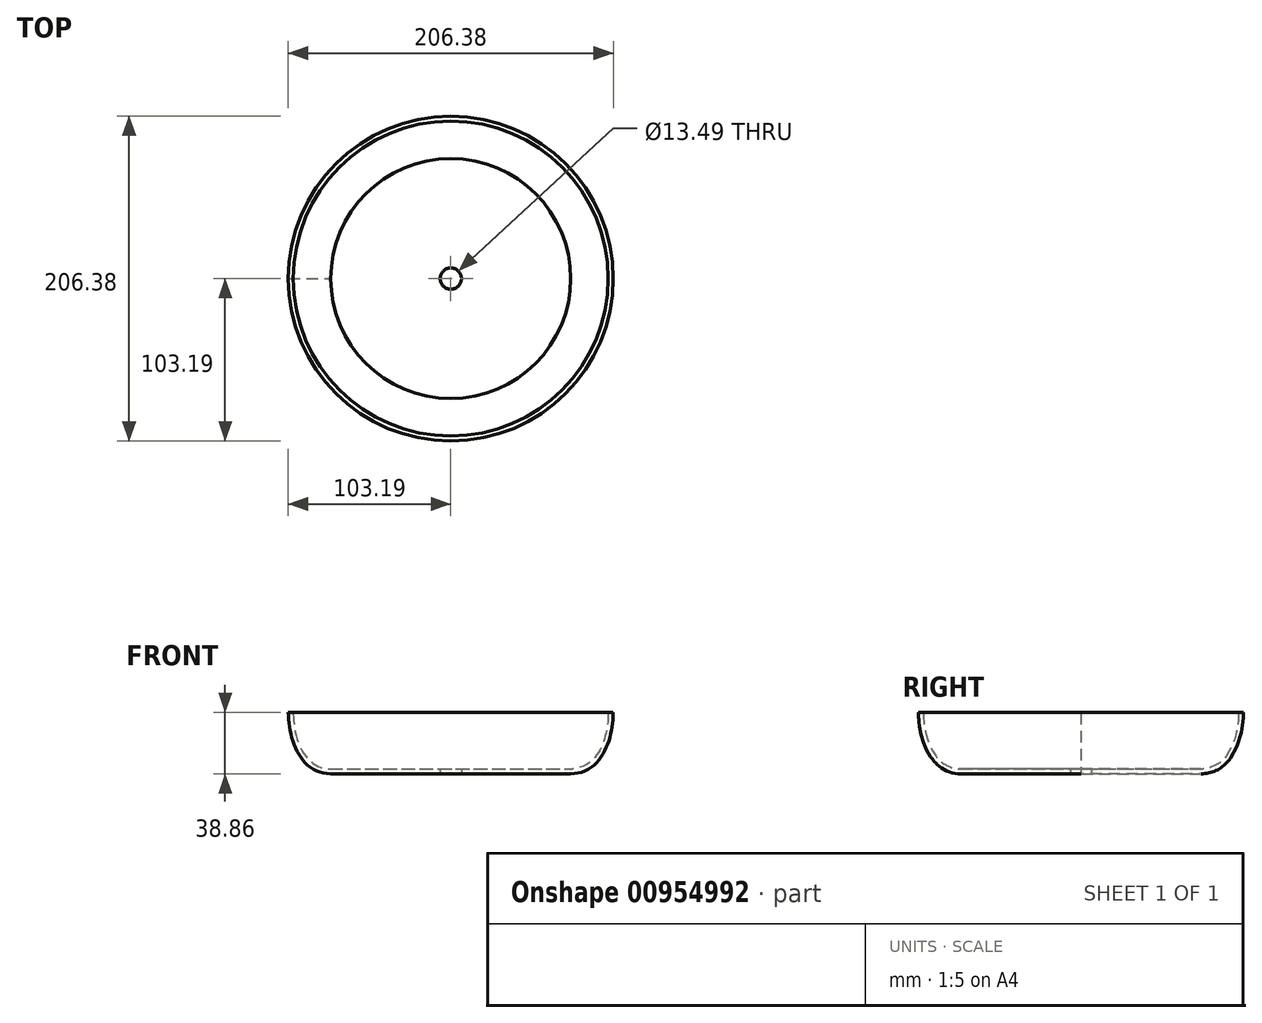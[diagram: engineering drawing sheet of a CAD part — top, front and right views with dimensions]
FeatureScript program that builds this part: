
annotation { "Feature Type Name" : "Feature", "Feature Type Description" : "" }
export const myFeature = defineFeature(function(context is Context, id is Id, definition is map)
    precondition{}
    {
        {
            var Q0;
            Q0=qCreatedBy(makeId("Top.planeOp"),FACE);
            var sketch = newSketch(context, id + "F0", { "sketchPlane" : qUnion([Q0])});
            skCircle(sketch, "E0", {"center": v(0, 0) * mm, "radius": 76.2 * mm});
            skSolve(sketch);
        }
        {
            var Q0;
            Q0 = qSketchRegion(id + "F0", true);
            extrude(context, id + "F1", {"entities" : qUnion([Q0]), "depth" : 3.17 * mm, "offsetDistance" : 25.4 * mm});
        }
        {
            var Q0;
            Q0=qCreatedBy(makeId("Top.planeOp"),FACE);
            cPlane(context, id + "F2", {"entities" : qUnion([Q0]), "cplaneType" : CPlaneType.OFFSET, "offset" : 38.86 * mm, "width" : 152.4 * mm, "height" : 152.4 * mm});
        }
        {
            var Q0;
            Q0=qCreatedBy(id+"F2.planeOp",FACE);
            var sketch = newSketch(context, id + "F3", { "sketchPlane" : qUnion([Q0])});
            skCircle(sketch, "E1", {"center": v(0, 0) * mm, "radius": 100.01 * mm});
            skCircle(sketch, "E2.0", {"center": v(0, 0) * mm, "radius": 103.19 * mm});
            skSolve(sketch);
        }
        {
            var Q0;
            Q0=qCreatedBy(makeId("Front.planeOp"),FACE);
            var sketch = newSketch(context, id + "F4", { "sketchPlane" : qUnion([Q0])});
            skFitSpline(sketch, "E3", {"points": [v(-103.19, 38.86) * mm, v(-76.2, 0) * mm], "startDerivative": vector(0, -49.38) * mm, "endDerivative": vector(58.66, 0) * mm});
            skLineSegment(sketch, "E4.0", {"start": v(-76.2, 0) * mm, "end": v(76.2, 0) * mm});
            skLineSegment(sketch, "E5.0", {"start": v(-103.19, 38.86) * mm, "end": v(103.19, 38.86) * mm, "construction": true});
            skFitSpline(sketch, "E6.0", {"points": [v(-100.01, 38.86) * mm, v(-100.01, 36.92) * mm, v(-99.8, 32.85) * mm, v(-98.75, 26.52) * mm, v(-96.95, 20.35) * mm, v(-94.39, 14.67) * mm, v(-91.05, 9.85) * mm, v(-87.68, 6.77) * mm, v(-84.6, 4.97) * mm, v(-81.23, 3.63) * mm, v(-78.34, 3.18) * mm, v(-76.2, 3.18) * mm]});
            skLineSegment(sketch, "E7", {"start": v(-103.19, 38.86) * mm, "end": v(-100.01, 38.86) * mm});
            skLineSegment(sketch, "E8", {"start": v(-76.2, 0) * mm, "end": v(-76.2, 3.18) * mm});
            skLineSegment(sketch, "E9", {"start": v(0, 0) * mm, "end": v(0, 60.06) * mm, "construction": true});
            skSolve(sketch);
        }
        {
            var Q0;
            Q0=makeQuery(id+"F4.imprint","IMPRINT",FACE,{"disambiguationData":[TD([[makeQuery(id+"F4.imprint","IMPRINT",EDGE,{"derivedFrom":sQuery(id+"F4.wireOp",EDGE,"E3")}),1.0]])]});
            var Q1;
            Q1=sQuery(id+"F4.wireOp",EDGE,"E9");
            revolve(context, id + "F5", {"operationType" : NewBodyOperationType.ADD, "surfaceOperationType" : NewSurfaceOperationType.NEW, "entities" : qUnion([Q0]), "axis" : qUnion([Q1]), "revolveType" : RevolveType.FULL});
        }
        {
            var Q0;
            Q0=sQuery(id+"F3.wireOp",VERTEX,"E1.center");
            var Q1;
            Q1=makeQuery(id+"F1.opExtrude","SWEPT_BODY",BODY,{"disambiguationData":[OSD([sQuery(id+"F0.wireOp",EDGE,"E0")])]});
            hole(context, id + "F6", {"style" : HoleStyle.SIMPLE, "endStyle" : HoleEndStyle.THROUGH, "holeDiameter" : 13.5 * mm, "majorDiameter" : 6.35 * mm, "isTappedThrough" : true, "tappedDepth" : 12.7 * mm, "tapClearance" : 3, "locations" : qUnion([Q0]), "scope" : qUnion([Q1]), "startStyle" : HoleStartStyle.PART});
        }
    });
